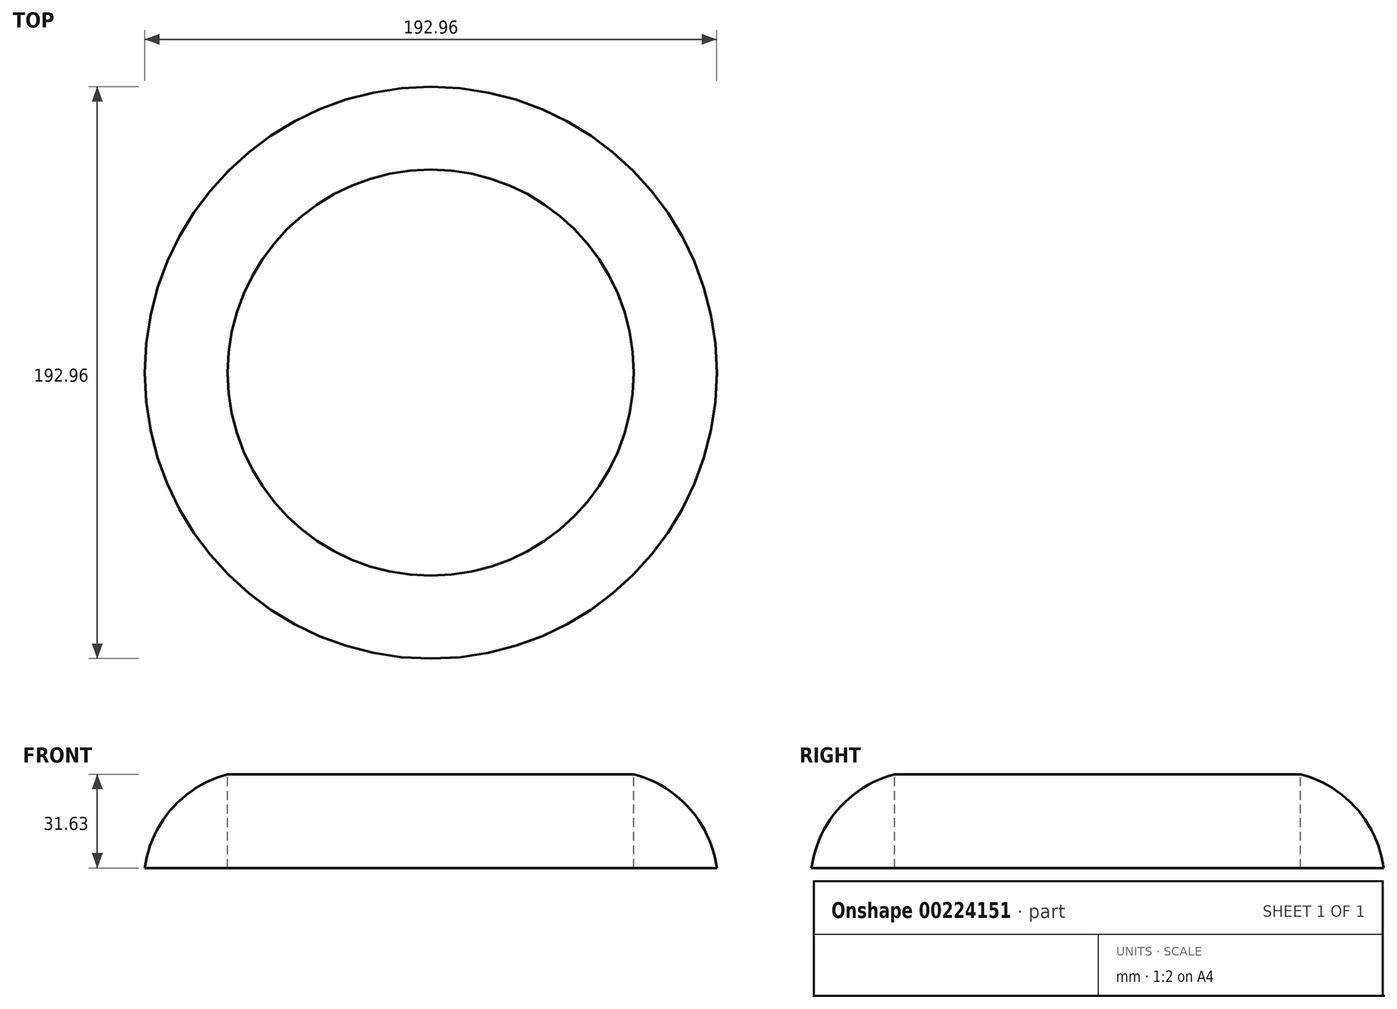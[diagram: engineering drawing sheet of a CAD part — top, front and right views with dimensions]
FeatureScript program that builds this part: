
annotation { "Feature Type Name" : "Feature", "Feature Type Description" : "" }
export const myFeature = defineFeature(function(context is Context, id is Id, definition is map)
    precondition{}
    {
        {
            var Q0;
            Q0=qCreatedBy(makeId("Front.planeOp"),FACE);
            var sketch = newSketch(context, id + "F0", { "sketchPlane" : qUnion([Q0])});
            skLineSegment(sketch, "E0", {"start": v(0, 31.63) * mm, "end": v(0, 0) * mm});
            skArc(sketch, "E1", {"start": v(27.98, 0) * mm, "mid": v(18.8, 20.07) * mm, "end": v(0, 31.63) * mm});
            skLineSegment(sketch, "E2", {"start": v(0, 0) * mm, "end": v(27.98, 0) * mm});
            skSolve(sketch);
        }
        {
            var Q0;
            Q0=qCreatedBy(makeId("Front.planeOp"),FACE);
            var sketch = newSketch(context, id + "F1", { "sketchPlane" : qUnion([Q0])});
            skLineSegment(sketch, "E3", {"start": v(-68.5, 36.58) * mm, "end": v(-68.5, -15.3) * mm});
            skSolve(sketch);
        }
        {
            var Q0;
            Q0=makeQuery(id+"F0.imprint","IMPRINT",FACE,{"disambiguationData":[TD([[makeQuery(id+"F0.imprint","IMPRINT",EDGE,{"derivedFrom":sQuery(id+"F0.wireOp",EDGE,"E0")}),1.0]])]});
            var Q1;
            Q1=sQuery(id+"F1.wireOp",EDGE,"E3");
            revolve(context, id + "F2", {"entities" : qUnion([Q0]), "axis" : qUnion([Q1]), "revolveType" : RevolveType.FULL});
        }
    });
